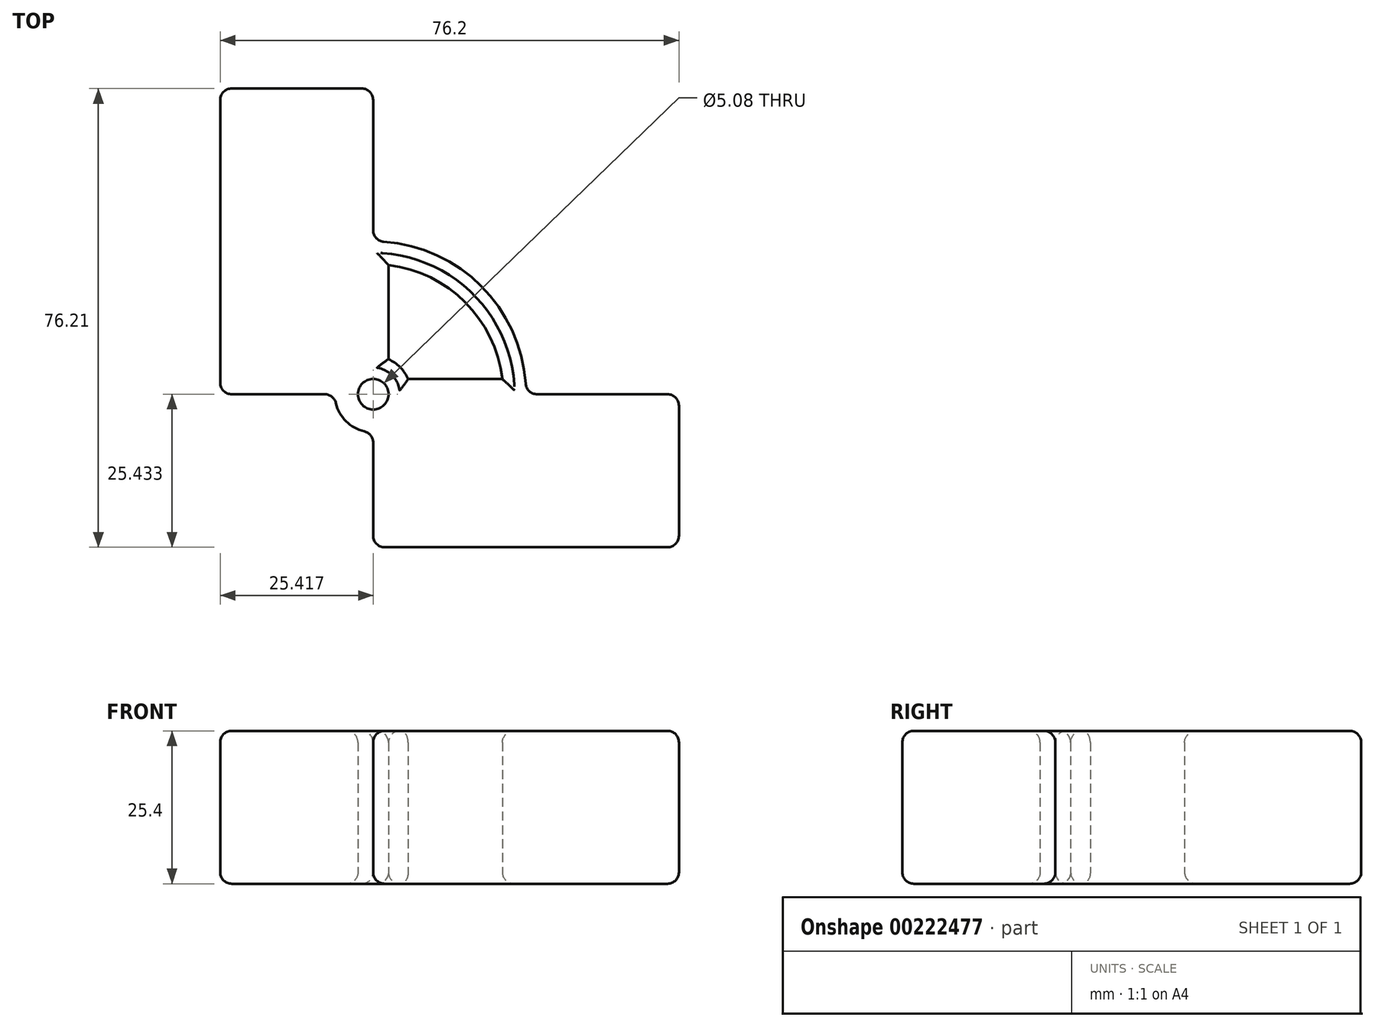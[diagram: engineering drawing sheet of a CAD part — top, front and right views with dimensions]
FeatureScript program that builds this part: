
annotation { "Feature Type Name" : "Feature", "Feature Type Description" : "" }
export const myFeature = defineFeature(function(context is Context, id is Id, definition is map)
    precondition{}
    {
        {
            var Q0;
            Q0=qCreatedBy(makeId("Top.planeOp"),FACE);
            var sketch = newSketch(context, id + "F0", { "sketchPlane" : qUnion([Q0])});
            skLineSegment(sketch, "E0.bottom", {"start": v(-54.1, 32.67) * mm, "end": v(-28.7, 32.67) * mm});
            skLineSegment(sketch, "E0.top", {"start": v(-54.1, -18.13) * mm, "end": v(-28.7, -18.13) * mm});
            skLineSegment(sketch, "E0.left", {"start": v(-54.1, 32.67) * mm, "end": v(-54.1, -18.13) * mm});
            skLineSegment(sketch, "E0.right", {"start": v(-28.7, 32.67) * mm, "end": v(-28.7, -18.13) * mm});
            skArc(sketch, "E1", {"start": v(-28.7, -43.53) * mm, "mid": v(-10.74, -0.16) * mm, "end": v(-54.1, -18.13) * mm});
            skLineSegment(sketch, "E2.bottom", {"start": v(-28.7, -18.13) * mm, "end": v(22.1, -18.13) * mm});
            skLineSegment(sketch, "E2.top", {"start": v(-28.7, -43.54) * mm, "end": v(22.1, -43.54) * mm});
            skLineSegment(sketch, "E2.left", {"start": v(-28.7, -18.13) * mm, "end": v(-28.7, -43.54) * mm});
            skLineSegment(sketch, "E2.right", {"start": v(22.1, -18.13) * mm, "end": v(22.1, -43.54) * mm});
            skCircle(sketch, "E3", {"center": v(-28.7, -18.13) * mm, "radius": 6.35 * mm});
            skLineSegment(sketch, "E4", {"start": v(-22.88, -15.59) * mm, "end": v(-7.24, -15.59) * mm});
            skPoint(sketch, "E5", {"position": v(-3.43, -15.59) * mm});
            skLineSegment(sketch, "E6", {"start": v(-26.16, -12.3) * mm, "end": v(-26.16, 3.34) * mm});
            skPoint(sketch, "E7", {"position": v(-26.16, 7.15) * mm});
            skArc(sketch, "E8", {"start": v(-7.24, -15.59) * mm, "mid": v(-13.42, -2.84) * mm, "end": v(-26.16, 3.34) * mm});
            skCircle(sketch, "E9", {"center": v(-28.68, -18.1) * mm, "radius": 2.54 * mm});
            skSolve(sketch);
        }
        {
            var Q0;
            {var subQ0=sQuery(id+"F0.wireOp",EDGE,"E0.bottom");Q0=makeQuery(id+"F0.imprint","IMPRINT",FACE,{"disambiguationData":[TD([[makeQuery(id+"F0.imprint","IMPRINT",EDGE,{"derivedFrom":subQ0}),-1.0]])]});}
            var Q1;
            {var subQ0=sQuery(id+"F0.wireOp",EDGE,"E1");var subQ5=sQuery(id+"F0.wireOp",EDGE,"E0.right");var subQ6=makeQuery(id+"F0.imprint","INTERSECT",VERTEX,{"derivedFrom":[subQ5,subQ0]});Q1=makeQuery(id+"F0.imprint","IMPRINT",FACE,{"disambiguationData":[TD([[makeQuery(id+"F0.imprint","IMPRINT",EDGE,{"disambiguationData":[TD([[subQ6,-1.0]])],"derivedFrom":subQ5}),-1.0]])]});}
            var Q2;
            {var subQ0=sQuery(id+"F0.wireOp",EDGE,"E4");Q2=makeQuery(id+"F0.imprint","IMPRINT",FACE,{"disambiguationData":[TD([[makeQuery(id+"F0.imprint","IMPRINT",EDGE,{"derivedFrom":subQ0}),-1.0]])]});}
            var Q3;
            {var subQ0=sQuery(id+"F0.wireOp",EDGE,"E2.left");var subQ1=sQuery(id+"F0.wireOp",EDGE,"E1");var subQ2=makeQuery(id+"F0.imprint","INTERSECT",VERTEX,{"derivedFrom":[subQ1,subQ0]});Q3=makeQuery(id+"F0.imprint","IMPRINT",FACE,{"disambiguationData":[TD([[makeQuery(id+"F0.imprint","IMPRINT",EDGE,{"disambiguationData":[TD([[subQ2,-1.0]])],"derivedFrom":subQ1}),1.0]])]});}
            var Q4;
            {var subQ3=sQuery(id+"F0.wireOp",EDGE,"E2.top");Q4=makeQuery(id+"F0.imprint","IMPRINT",FACE,{"disambiguationData":[TD([[makeQuery(id+"F0.imprint","IMPRINT",EDGE,{"derivedFrom":subQ3}),1.0]])]});}
            var Q5;
            {var subQ0=sQuery(id+"F0.wireOp",EDGE,"E2.left");var subQ3=sQuery(id+"F0.wireOp",EDGE,"E3");var subQ5=makeQuery(id+"F0.imprint","INTERSECT",VERTEX,{"derivedFrom":[subQ0,subQ3]});Q5=makeQuery(id+"F0.imprint","IMPRINT",FACE,{"disambiguationData":[TD([[makeQuery(id+"F0.imprint","IMPRINT",EDGE,{"disambiguationData":[TD([[subQ5,-1.0]])],"derivedFrom":subQ3}),1.0]])]});}
            var Q6;
            {var subQ0=sQuery(id+"F0.wireOp",EDGE,"E3");var subQ1=makeQuery(id+"F0.imprint","INTERSECT",VERTEX,{"derivedFrom":[subQ0,sQuery(id+"F0.wireOp",EDGE,"E4")]});Q6=makeQuery(id+"F0.imprint","IMPRINT",FACE,{"disambiguationData":[TD([[makeQuery(id+"F0.imprint","IMPRINT",EDGE,{"disambiguationData":[TD([[subQ1,1.0]])],"derivedFrom":subQ0}),1.0]])]});}
            var Q7;
            {var subQ1=sQuery(id+"F0.wireOp",EDGE,"E0.top");var subQ3=sQuery(id+"F0.wireOp",EDGE,"E3");var subQ4=makeQuery(id+"F0.imprint","INTERSECT",VERTEX,{"derivedFrom":[subQ1,subQ3]});Q7=makeQuery(id+"F0.imprint","IMPRINT",FACE,{"disambiguationData":[TD([[makeQuery(id+"F0.imprint","IMPRINT",EDGE,{"disambiguationData":[TD([[subQ4,1.0]])],"derivedFrom":subQ3}),1.0]])]});}
            var Q8;
            {var subQ1=sQuery(id+"F0.wireOp",EDGE,"E0.top");var subQ3=sQuery(id+"F0.wireOp",EDGE,"E3");var subQ4=makeQuery(id+"F0.imprint","INTERSECT",VERTEX,{"derivedFrom":[subQ1,subQ3]});Q8=makeQuery(id+"F0.imprint","IMPRINT",FACE,{"disambiguationData":[TD([[makeQuery(id+"F0.imprint","IMPRINT",EDGE,{"disambiguationData":[TD([[subQ4,-1.0]])],"derivedFrom":subQ3}),1.0]])]});}
            extrude(context, id + "F1", {"entities" : qUnion([Q0, Q1, Q2, Q3, Q4, Q5, Q6, Q7, Q8]), "depth" : 25.4 * mm});
        }
        {
            var Q0;
            Q0=makeQuery(id+"F1.opExtrude","CAP_EDGE",EDGE,{"disambiguationData":[OSD([sQuery(id+"F0.wireOp",EDGE,"E0.right")])],"isStart":false});
            var Q1;
            Q1=makeQuery(id+"F1.opExtrude","CAP_EDGE",EDGE,{"disambiguationData":[OSD([sQuery(id+"F0.wireOp",EDGE,"E0.bottom")])],"isStart":false});
            var Q2;
            Q2=makeQuery(id+"F1.opExtrude","CAP_EDGE",EDGE,{"disambiguationData":[OSD([sQuery(id+"F0.wireOp",EDGE,"E0.left")])],"isStart":false});
            var Q3;
            Q3=makeQuery(id+"F1.opExtrude","CAP_EDGE",EDGE,{"disambiguationData":[OSD([sQuery(id+"F0.wireOp",EDGE,"E0.top")])],"isStart":false});
            var Q4;
            {var subQ0=sQuery(id+"F0.wireOp",EDGE,"E3");Q4=makeQuery(id+"F1.opExtrude","CAP_EDGE",EDGE,{"disambiguationData":[OSD([subQ0]),TDD([makeQuery(id+"F0.imprint","IMPRINT",EDGE,{"disambiguationData":[TD([[makeQuery(id+"F0.imprint","INTERSECT",VERTEX,{"derivedFrom":[sQuery(id+"F0.wireOp",EDGE,"E0.top"),subQ0]}),-1.0]])],"derivedFrom":subQ0})])],"isStart":false});}
            var Q5;
            Q5=makeQuery(id+"F1.opExtrude","CAP_EDGE",EDGE,{"disambiguationData":[OSD([sQuery(id+"F0.wireOp",EDGE,"E2.left")])],"isStart":false});
            var Q6;
            Q6=makeQuery(id+"F1.opExtrude","CAP_EDGE",EDGE,{"disambiguationData":[OSD([sQuery(id+"F0.wireOp",EDGE,"E2.top")])],"isStart":false});
            var Q7;
            Q7=makeQuery(id+"F1.opExtrude","CAP_EDGE",EDGE,{"disambiguationData":[OSD([sQuery(id+"F0.wireOp",EDGE,"E2.right")])],"isStart":false});
            var Q8;
            Q8=makeQuery(id+"F1.opExtrude","CAP_EDGE",EDGE,{"disambiguationData":[OSD([sQuery(id+"F0.wireOp",EDGE,"E2.bottom")])],"isStart":false});
            var Q9;
            Q9=makeQuery(id+"F1.opExtrude","CAP_EDGE",EDGE,{"disambiguationData":[OSD([sQuery(id+"F0.wireOp",EDGE,"E1")])],"isStart":false});
            var Q10;
            Q10=makeQuery(id+"F1.opExtrude","CAP_EDGE",EDGE,{"disambiguationData":[OSD([sQuery(id+"F0.wireOp",EDGE,"E8")])],"isStart":false});
            var Q11;
            Q11=makeQuery(id+"F1.opExtrude","CAP_EDGE",EDGE,{"disambiguationData":[OSD([sQuery(id+"F0.wireOp",EDGE,"E4")])],"isStart":false});
            var Q12;
            Q12=makeQuery(id+"F1.opExtrude","CAP_EDGE",EDGE,{"disambiguationData":[OSD([sQuery(id+"F0.wireOp",EDGE,"E6")])],"isStart":false});
            var Q13;
            {var subQ0=sQuery(id+"F0.wireOp",EDGE,"E3");Q13=makeQuery(id+"F1.opExtrude","CAP_EDGE",EDGE,{"disambiguationData":[OSD([subQ0]),TDD([makeQuery(id+"F0.imprint","IMPRINT",EDGE,{"disambiguationData":[TD([[makeQuery(id+"F0.imprint","INTERSECT",VERTEX,{"derivedFrom":[subQ0,sQuery(id+"F0.wireOp",EDGE,"E4")]}),-1.0]])],"derivedFrom":subQ0})])],"isStart":false});}
            var Q14;
            Q14=makeQuery(id+"F1.opExtrude","CAP_EDGE",EDGE,{"disambiguationData":[OSD([sQuery(id+"F0.wireOp",EDGE,"E8")])],"isStart":true});
            var Q15;
            Q15=makeQuery(id+"F1.opExtrude","CAP_EDGE",EDGE,{"disambiguationData":[OSD([sQuery(id+"F0.wireOp",EDGE,"E4")])],"isStart":true});
            var Q16;
            {var subQ0=sQuery(id+"F0.wireOp",EDGE,"E3");Q16=makeQuery(id+"F1.opExtrude","CAP_EDGE",EDGE,{"disambiguationData":[OSD([subQ0]),TDD([makeQuery(id+"F0.imprint","IMPRINT",EDGE,{"disambiguationData":[TD([[makeQuery(id+"F0.imprint","INTERSECT",VERTEX,{"derivedFrom":[subQ0,sQuery(id+"F0.wireOp",EDGE,"E4")]}),-1.0]])],"derivedFrom":subQ0})])],"isStart":true});}
            var Q17;
            Q17=makeQuery(id+"F1.opExtrude","CAP_EDGE",EDGE,{"disambiguationData":[OSD([sQuery(id+"F0.wireOp",EDGE,"E6")])],"isStart":true});
            var Q18;
            Q18=makeQuery(id+"F1.opExtrude","CAP_EDGE",EDGE,{"disambiguationData":[OSD([sQuery(id+"F0.wireOp",EDGE,"E9")])],"isStart":false});
            var Q19;
            Q19=makeQuery(id+"F1.opExtrude","CAP_EDGE",EDGE,{"disambiguationData":[OSD([sQuery(id+"F0.wireOp",EDGE,"E2.top")])],"isStart":true});
            var Q20;
            Q20=makeQuery(id+"F1.opExtrude","CAP_EDGE",EDGE,{"disambiguationData":[OSD([sQuery(id+"F0.wireOp",EDGE,"E2.left")])],"isStart":true});
            var Q21;
            Q21=makeQuery(id+"F1.opExtrude","CAP_FACE",FACE,{"disambiguationData":[OSD([sQuery(id+"F0.wireOp",EDGE,"E0.bottom"),sQuery(id+"F0.wireOp",EDGE,"E0.top"),sQuery(id+"F0.wireOp",EDGE,"E0.left"),sQuery(id+"F0.wireOp",EDGE,"E0.right"),sQuery(id+"F0.wireOp",EDGE,"E1"),sQuery(id+"F0.wireOp",EDGE,"E2.bottom"),sQuery(id+"F0.wireOp",EDGE,"E2.top"),sQuery(id+"F0.wireOp",EDGE,"E2.left"),sQuery(id+"F0.wireOp",EDGE,"E2.right"),sQuery(id+"F0.wireOp",EDGE,"E3"),sQuery(id+"F0.wireOp",EDGE,"E4"),sQuery(id+"F0.wireOp",EDGE,"E6"),sQuery(id+"F0.wireOp",EDGE,"E8"),sQuery(id+"F0.wireOp",EDGE,"E9")])],"isStart":true});
            var Q22;
            Q22=makeQuery(id+"F1.opExtrude","SWEPT_FACE",FACE,{"disambiguationData":[OSD([sQuery(id+"F0.wireOp",EDGE,"E2.top")])]});
            var Q23;
            Q23=makeQuery(id+"F1.opExtrude","SWEPT_FACE",FACE,{"disambiguationData":[OSD([sQuery(id+"F0.wireOp",EDGE,"E2.left")])]});
            var Q24;
            {var subQ0=sQuery(id+"F0.wireOp",EDGE,"E3");Q24=makeQuery(id+"F1.opExtrude","SWEPT_FACE",FACE,{"disambiguationData":[OSD([subQ0]),TDD([makeQuery(id+"F0.imprint","IMPRINT",EDGE,{"disambiguationData":[TD([[makeQuery(id+"F0.imprint","INTERSECT",VERTEX,{"derivedFrom":[sQuery(id+"F0.wireOp",EDGE,"E0.top"),subQ0]}),-1.0]])],"derivedFrom":subQ0})])]});}
            var Q25;
            Q25=makeQuery(id+"F1.opExtrude","SWEPT_FACE",FACE,{"disambiguationData":[OSD([sQuery(id+"F0.wireOp",EDGE,"E0.top")])]});
            var Q26;
            Q26=makeQuery(id+"F1.opExtrude","SWEPT_FACE",FACE,{"disambiguationData":[OSD([sQuery(id+"F0.wireOp",EDGE,"E0.left")])]});
            var Q27;
            Q27=makeQuery(id+"F1.opExtrude","SWEPT_FACE",FACE,{"disambiguationData":[OSD([sQuery(id+"F0.wireOp",EDGE,"E0.right")])]});
            var Q28;
            Q28=makeQuery(id+"F1.opExtrude","SWEPT_FACE",FACE,{"disambiguationData":[OSD([sQuery(id+"F0.wireOp",EDGE,"E2.bottom")])]});
            fillet(context, id + "F2", {"entities" : qUnion([Q0, Q1, Q2, Q3, Q4, Q5, Q6, Q7, Q8, Q9, Q10, Q11, Q12, Q13, Q14, Q15, Q16, Q17, Q18, Q19, Q20, Q21, Q22, Q23, Q24, Q25, Q26, Q27, Q28]), "radius" : 1.9 * mm, "tangentPropagation" : true, "allowEdgeOverflow" : false});
        }
    });
